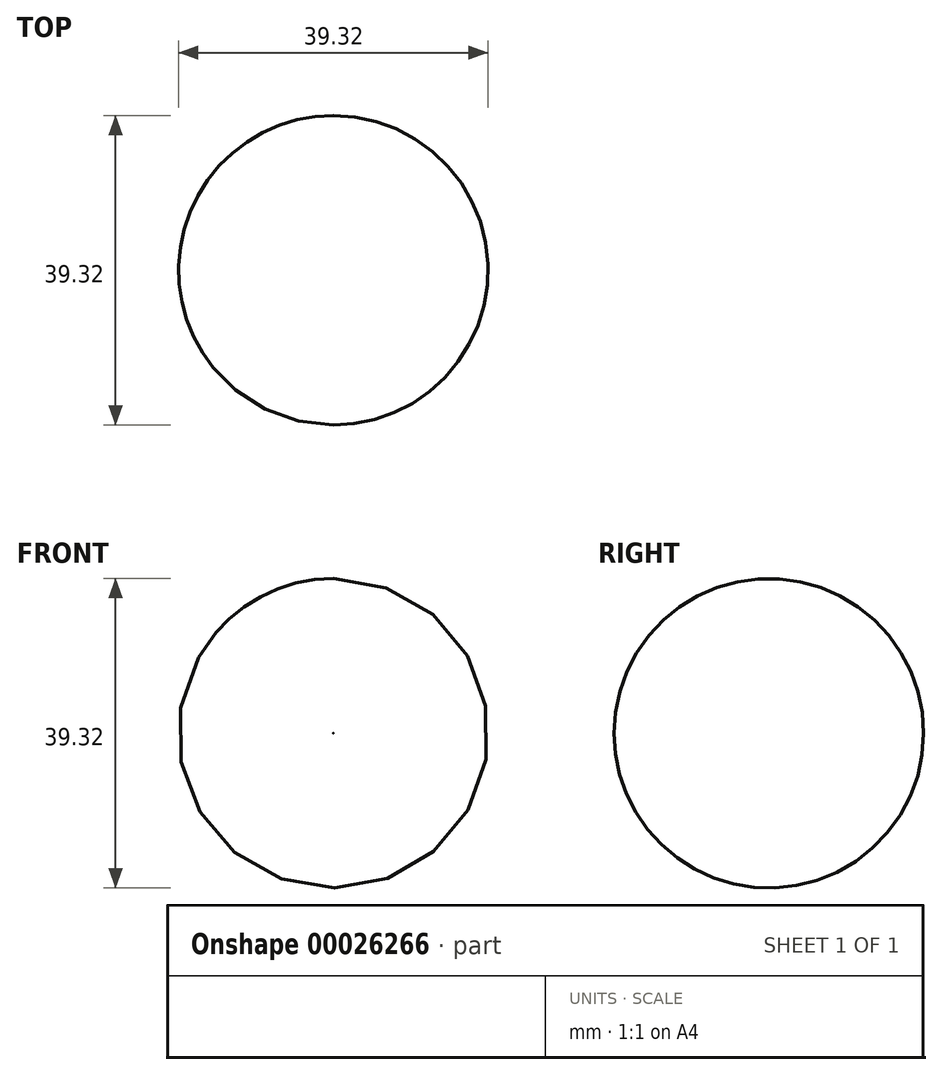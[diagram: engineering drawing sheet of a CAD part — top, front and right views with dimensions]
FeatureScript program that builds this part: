
annotation { "Feature Type Name" : "Feature", "Feature Type Description" : "" }
export const myFeature = defineFeature(function(context is Context, id is Id, definition is map)
    precondition{}
    {
        {
            var Q0;
            Q0=qCreatedBy(makeId("Top.planeOp"),FACE);
            var sketch = newSketch(context, id + "F0", { "sketchPlane" : qUnion([Q0])});
            skCircle(sketch, "E0", {"center": v(0, 0) * mm, "radius": 12.7 * mm});
            skLineSegment(sketch, "E1", {"start": v(0, 0) * mm, "end": v(25.4, 0) * mm});
            skLineSegment(sketch, "E2", {"start": v(25.4, 0) * mm, "end": v(25.4, 22.97) * mm});
            skSolve(sketch);
        }
        {
            var Q0;
            Q0=qCreatedBy(makeId("Front.planeOp"),FACE);
            var sketch = newSketch(context, id + "F1", { "sketchPlane" : qUnion([Q0])});
            skCircle(sketch, "E3", {"center": v(0, -12.7) * mm, "radius": 19.66 * mm});
            skLineSegment(sketch, "E4", {"start": v(0, 0) * mm, "end": v(0, -12.7) * mm});
            skSolve(sketch);
        }
        {
            var Q0;
            Q0=makeQuery(id+"F1.imprint","IMPRINT",FACE,{"disambiguationData":[TD([[makeQuery(id+"F1.imprint","IMPRINT",EDGE,{"derivedFrom":sQuery(id+"F1.wireOp",EDGE,"E3")}),1.0]])]});
            extrude(context, id + "F2", {"entities" : qUnion([Q0]), "endBound" : BoundingType.SYMMETRIC, "depth" : 39.32 * mm});
        }
        {
            var Q0;
            Q0=makeQuery(id+"F2.opExtrude","CAP_FACE",FACE,{"disambiguationData":[OSD([sQuery(id+"F1.wireOp",EDGE,"E3")])],"isStart":true});
            var Q1;
            Q1=makeQuery(id+"F2.opExtrude","CAP_FACE",FACE,{"disambiguationData":[OSD([sQuery(id+"F1.wireOp",EDGE,"E3")])],"isStart":false});
            fillet(context, id + "F3", {"entities" : qUnion([Q0, Q1]), "radius" : 19.66 * mm, "tangentPropagation" : true, "allowEdgeOverflow" : false});
        }
        {
            var Q0;
            Q0 = qSketchRegion(id + "F0", true);
            extrude(context, id + "F4", {"entities" : qUnion([Q0]), "operationType" : NewBodyOperationType.ADD, "depth" : 25.4 * mm});
        }
    });
